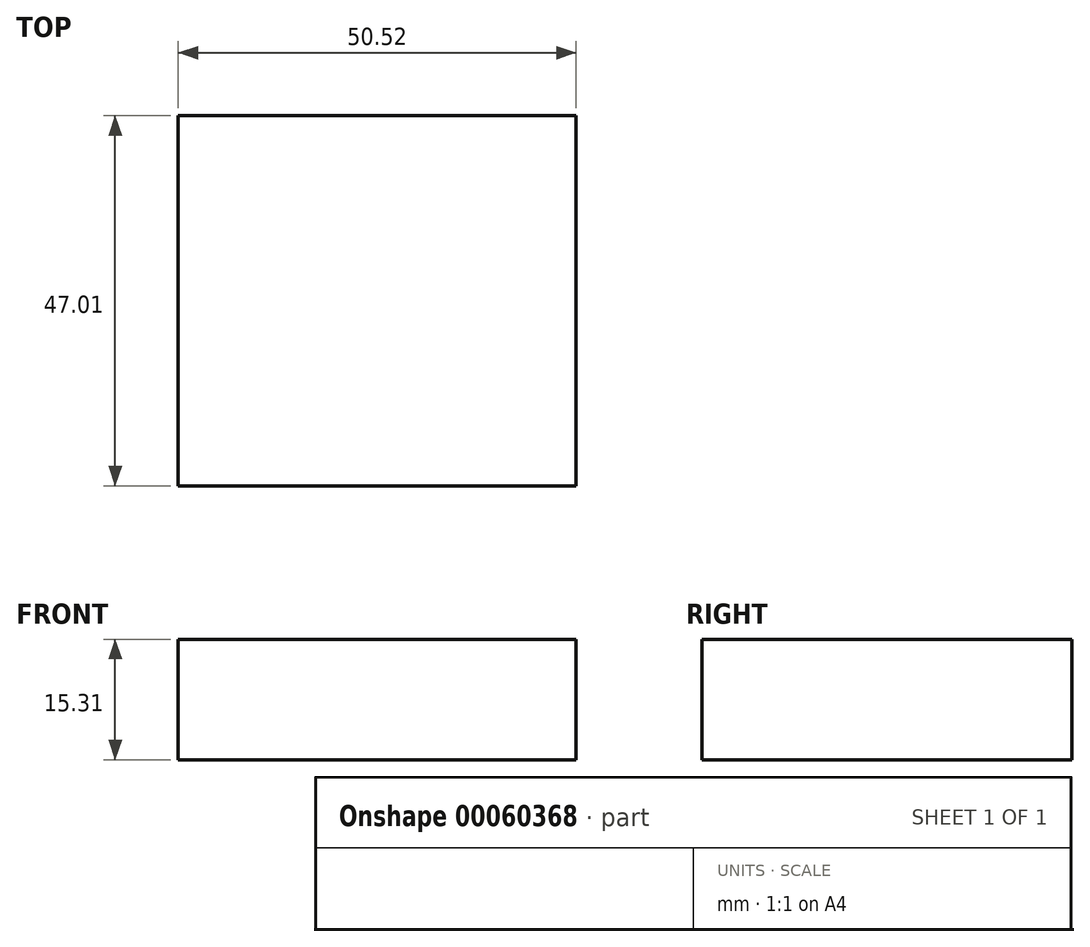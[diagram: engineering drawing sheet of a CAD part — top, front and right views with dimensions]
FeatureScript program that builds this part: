
annotation { "Feature Type Name" : "Feature", "Feature Type Description" : "" }
export const myFeature = defineFeature(function(context is Context, id is Id, definition is map)
    precondition{}
    {
        {
            var Q0;
            Q0=qCreatedBy(makeId("Top.planeOp"),FACE);
            var sketch = newSketch(context, id + "F0", { "sketchPlane" : qUnion([Q0])});
            skLineSegment(sketch, "E0.bottom", {"start": v(-25.34, 21.83) * mm, "end": v(25.18, 21.83) * mm});
            skLineSegment(sketch, "E0.top", {"start": v(-25.34, -25.18) * mm, "end": v(25.18, -25.18) * mm});
            skLineSegment(sketch, "E0.left", {"start": v(-25.34, 21.83) * mm, "end": v(-25.34, -25.18) * mm});
            skLineSegment(sketch, "E0.right", {"start": v(25.18, 21.83) * mm, "end": v(25.18, -25.18) * mm});
            skSolve(sketch);
        }
        {
            var Q0;
            Q0=makeQuery(id+"F0.imprint","IMPRINT",FACE,{"disambiguationData":[TD([[makeQuery(id+"F0.imprint","IMPRINT",EDGE,{"derivedFrom":sQuery(id+"F0.wireOp",EDGE,"E0.bottom")}),-1.0]])]});
            extrude(context, id + "F1", {"entities" : qUnion([Q0]), "depth" : 15.3 * mm});
        }
    });
